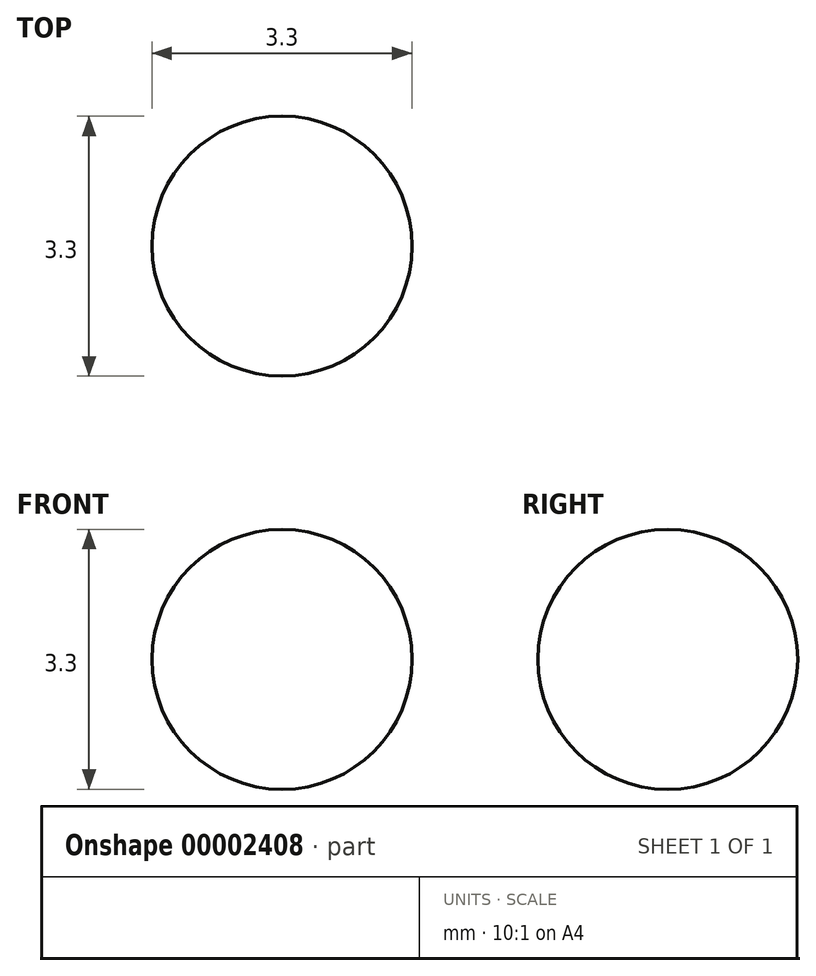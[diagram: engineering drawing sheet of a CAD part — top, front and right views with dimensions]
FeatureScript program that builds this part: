
annotation { "Feature Type Name" : "Feature", "Feature Type Description" : "" }
export const myFeature = defineFeature(function(context is Context, id is Id, definition is map)
    precondition{}
    {
        {
            var Q0;
            Q0=qCreatedBy(makeId("Top.planeOp"),FACE);
            var sketch = newSketch(context, id + "F0", { "sketchPlane" : qUnion([Q0])});
            skArc(sketch, "E0", {"start": v(0, 1.65) * mm, "mid": v(-1.65, 0) * mm, "end": v(0, -1.65) * mm});
            skLineSegment(sketch, "E1", {"start": v(0, -2.23) * mm, "end": v(0, 2.17) * mm, "construction": true});
            skLineSegment(sketch, "E2", {"start": v(0, -1.65) * mm, "end": v(0, 1.65) * mm});
            skSolve(sketch);
        }
        {
            var Q0;
            Q0=qSketchRegion(id+"F0",true);
            var Q1;
            Q1=sQuery(id+"F0.wireOp",EDGE,"E1");
            revolve(context, id + "F1", {"entities" : qUnion([Q0]), "axis" : qUnion([Q1]), "revolveType" : RevolveType.FULL});
        }
    });
